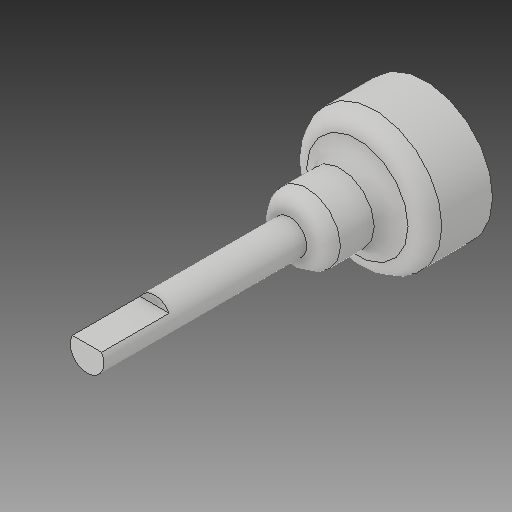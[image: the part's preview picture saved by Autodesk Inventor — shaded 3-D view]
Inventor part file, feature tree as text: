
AUTODESK INVENTOR PART (.ipt)
format: ipt  version: 2019 (Build 230136000, 136)  size: 164,864 bytes
history: native  units: in
note: dims shown in document units (in); Inventor stores cm internally (conversion verified against a paired STEP export)
features: sketch x6, extrude x5, fillet x3, thicken_offset x2, hole x1, plane x1
ambient origin geometry x8: Origin, YZ Plane, XZ Plane, XY Plane, X Axis, Y Axis, Z Axis, Center Point
bodies: Solid1 (feature_tree)
feature tree (18):
  sketch  "Sketch1"  dims[d0=1.0in d1=0.5in]
  extrude  "Extrusion1"  Depth=0.5in
  extrude  "Extrusion2"  Depth=1.0in TaperAngle=0.0deg
  fillet  "Fillet1"  Radius=0.125in
  fillet  "Fillet2"  Radius=0.125in
  extrude  "Extrusion3"  Depth=0.25in TaperAngle=0.0deg
  extrude  "Extrusion4"  Depth=0.125in TaperAngle=0.0deg
  fillet  "Fillet3"  Radius=0.125in
  extrude  "Extrusion6"  Depth=0.0625in TaperAngle=0.0deg
  hole  "Hole1"  [1 undecoded]
  sketch  "Sketch8"  dims[d23=0.125in d24=0.75in d25=0.375in d26=0.25in d27=0.5635in d28=1.0in d29=0.8108in d32=0.15in d35=9.0in d36=9.0in d37=5.0in d38=5.0in]
  plane  "Work Plane3"
  thicken_offset  "Thicken1"
  thicken_offset  "Thicken2"
  sketch  "Sketch3"  dims[d2=0.5in d3=0.0in d4=1.0in d5=0.0in d6=0.125in d7=0.125in]
  sketch  "Sketch4"  dims[d8=0.25in d9=10.5in d10=0.0in]
  sketch  "Sketch6"  dims[d11=0.0625in d12=4.5in d13=0.0in d17=0.125in]
  sketch  "Sketch7"  dims[d18=0.1875in d19=0.0625in d20=0.0in]
note: 1 required parameter value undecoded (feature->parameter linkage not recoverable at this tier; creation-order binding heuristic only, values carry confidence <= 0.55)
